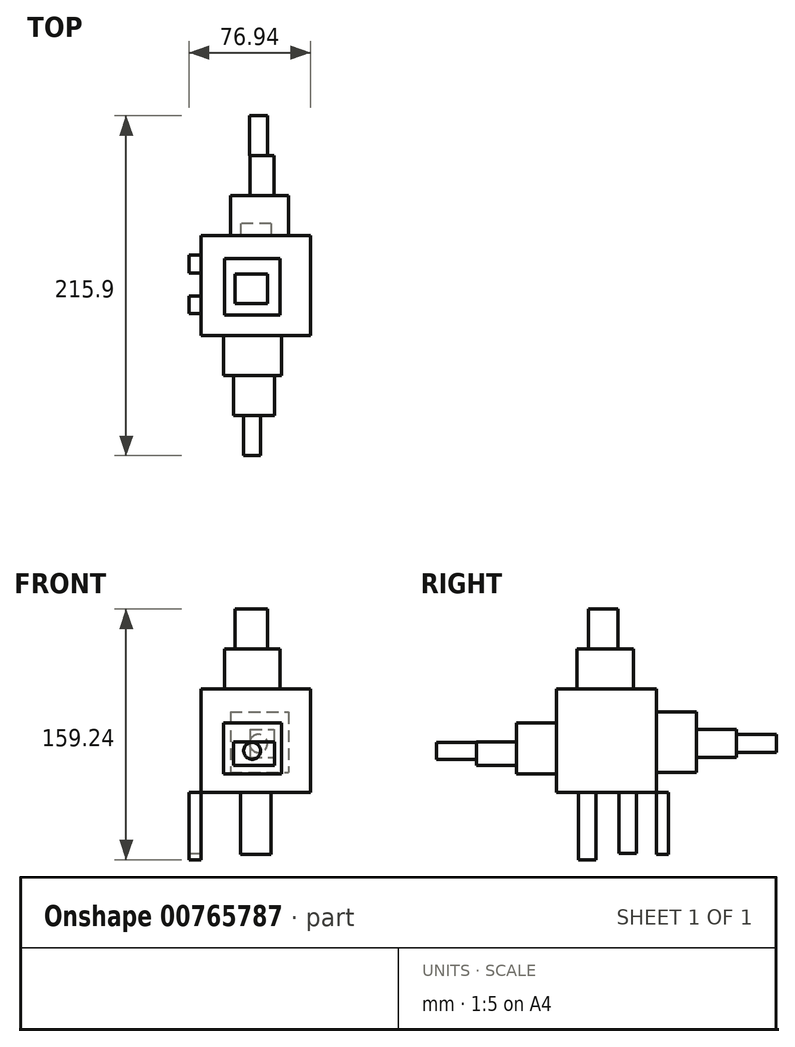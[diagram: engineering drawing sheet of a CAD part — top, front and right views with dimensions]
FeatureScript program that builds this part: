
annotation { "Feature Type Name" : "Feature", "Feature Type Description" : "" }
export const myFeature = defineFeature(function(context is Context, id is Id, definition is map)
    precondition{}
    {
        {
            var Q0;
            Q0=qCreatedBy(makeId("Front.planeOp"),FACE);
            var sketch = newSketch(context, id + "F0", { "sketchPlane" : qUnion([Q0])});
            skLineSegment(sketch, "E0.bottom", {"start": v(0, 0) * mm, "end": v(-69.32, 0) * mm});
            skLineSegment(sketch, "E0.top", {"start": v(0, 65.58) * mm, "end": v(-69.32, 65.58) * mm});
            skLineSegment(sketch, "E0.left", {"start": v(0, 0) * mm, "end": v(0, 65.58) * mm});
            skLineSegment(sketch, "E0.right", {"start": v(-69.32, 0) * mm, "end": v(-69.32, 65.58) * mm});
            skSolve(sketch);
        }
        {
            var Q0;
            Q0 = qSketchRegion(id + "F0", true);
            extrude(context, id + "F1", {"entities" : qUnion([Q0]), "depth" : 63.5 * mm, "offsetDistance" : 25.4 * mm});
        }
        {
            var Q0;
            Q0=makeQuery(id+"F1.opExtrude","SWEPT_FACE",FACE,{"disambiguationData":[OSD([sQuery(id+"F0.wireOp",EDGE,"E0.top")])]});
            var sketch = newSketch(context, id + "F2", { "sketchPlane" : qUnion([Q0])});
            skLineSegment(sketch, "E1.bottom", {"start": v(-54.41, -14.4) * mm, "end": v(-19.32, -14.4) * mm});
            skLineSegment(sketch, "E1.top", {"start": v(-54.41, -50.4) * mm, "end": v(-19.32, -50.4) * mm});
            skLineSegment(sketch, "E1.left", {"start": v(-54.41, -14.4) * mm, "end": v(-54.41, -50.4) * mm});
            skLineSegment(sketch, "E1.right", {"start": v(-19.32, -14.4) * mm, "end": v(-19.32, -50.4) * mm});
            skSolve(sketch);
        }
        {
            var Q0;
            Q0 = qSketchRegion(id + "F2", true);
            extrude(context, id + "F3", {"entities" : qUnion([Q0]), "operationType" : NewBodyOperationType.ADD, "depth" : 25.4 * mm, "offsetDistance" : 25.4 * mm});
        }
        {
            var Q0;
            Q0=makeQuery(id+"F3.opExtrude","CAP_FACE",FACE,{"disambiguationData":[OSD([sQuery(id+"F2.wireOp",EDGE,"E1.bottom"),sQuery(id+"F2.wireOp",EDGE,"E1.top"),sQuery(id+"F2.wireOp",EDGE,"E1.left"),sQuery(id+"F2.wireOp",EDGE,"E1.right")])],"isStart":false});
            var sketch = newSketch(context, id + "F4", { "sketchPlane" : qUnion([Q0])});
            skLineSegment(sketch, "E2.bottom", {"start": v(-47.96, -24.32) * mm, "end": v(-27.13, -24.32) * mm});
            skLineSegment(sketch, "E2.top", {"start": v(-47.96, -42.99) * mm, "end": v(-27.13, -42.99) * mm});
            skLineSegment(sketch, "E2.left", {"start": v(-47.96, -24.32) * mm, "end": v(-47.96, -42.99) * mm});
            skLineSegment(sketch, "E2.right", {"start": v(-27.13, -24.32) * mm, "end": v(-27.13, -42.99) * mm});
            skSolve(sketch);
        }
        {
            var Q0;
            Q0 = qSketchRegion(id + "F4", true);
            extrude(context, id + "F5", {"entities" : qUnion([Q0]), "operationType" : NewBodyOperationType.ADD, "depth" : 25.4 * mm, "offsetDistance" : 25.4 * mm});
        }
        {
            var Q0;
            Q0=makeQuery(id+"F1.opExtrude","CAP_FACE",FACE,{"disambiguationData":[OSD([sQuery(id+"F0.wireOp",EDGE,"E0.bottom"),sQuery(id+"F0.wireOp",EDGE,"E0.top"),sQuery(id+"F0.wireOp",EDGE,"E0.left"),sQuery(id+"F0.wireOp",EDGE,"E0.right")])],"isStart":false});
            var sketch = newSketch(context, id + "F6", { "sketchPlane" : qUnion([Q0])});
            skLineSegment(sketch, "E3.bottom", {"start": v(-55.1, 44.17) * mm, "end": v(-18.17, 44.17) * mm});
            skLineSegment(sketch, "E3.top", {"start": v(-55.1, 11.61) * mm, "end": v(-18.17, 11.61) * mm});
            skLineSegment(sketch, "E3.left", {"start": v(-55.1, 44.17) * mm, "end": v(-55.1, 11.61) * mm});
            skLineSegment(sketch, "E3.right", {"start": v(-18.17, 44.17) * mm, "end": v(-18.17, 11.61) * mm});
            skSolve(sketch);
        }
        {
            var Q0;
            Q0 = qSketchRegion(id + "F6", true);
            extrude(context, id + "F7", {"entities" : qUnion([Q0]), "operationType" : NewBodyOperationType.ADD, "depth" : 25.4 * mm, "offsetDistance" : 25.4 * mm});
        }
        {
            var Q0;
            Q0=makeQuery(id+"F7.opExtrude","CAP_FACE",FACE,{"disambiguationData":[OSD([sQuery(id+"F6.wireOp",EDGE,"E3.bottom"),sQuery(id+"F6.wireOp",EDGE,"E3.top"),sQuery(id+"F6.wireOp",EDGE,"E3.left"),sQuery(id+"F6.wireOp",EDGE,"E3.right")])],"isStart":false});
            var sketch = newSketch(context, id + "F8", { "sketchPlane" : qUnion([Q0])});
            skLineSegment(sketch, "E4.bottom", {"start": v(-48.92, 32.12) * mm, "end": v(-22.66, 32.12) * mm});
            skLineSegment(sketch, "E4.top", {"start": v(-48.92, 17) * mm, "end": v(-22.66, 17) * mm});
            skLineSegment(sketch, "E4.left", {"start": v(-48.92, 32.12) * mm, "end": v(-48.92, 17) * mm});
            skLineSegment(sketch, "E4.right", {"start": v(-22.66, 32.12) * mm, "end": v(-22.66, 17) * mm});
            skSolve(sketch);
        }
        {
            var Q0;
            Q0 = qSketchRegion(id + "F8", true);
            extrude(context, id + "F9", {"entities" : qUnion([Q0]), "operationType" : NewBodyOperationType.ADD, "depth" : 25.4 * mm, "offsetDistance" : 25.4 * mm});
        }
        {
            var Q0;
            Q0=makeQuery(id+"F9.opExtrude","CAP_FACE",FACE,{"disambiguationData":[OSD([sQuery(id+"F8.wireOp",EDGE,"E4.bottom"),sQuery(id+"F8.wireOp",EDGE,"E4.top"),sQuery(id+"F8.wireOp",EDGE,"E4.left"),sQuery(id+"F8.wireOp",EDGE,"E4.right")])],"isStart":false});
            var sketch = newSketch(context, id + "F10", { "sketchPlane" : qUnion([Q0])});
            skCircle(sketch, "E5", {"center": v(-36.99, 26.38) * mm, "radius": 5.37 * mm});
            skSolve(sketch);
        }
        {
            var Q0;
            Q0 = qSketchRegion(id + "F10", true);
            extrude(context, id + "F11", {"entities" : qUnion([Q0]), "operationType" : NewBodyOperationType.ADD, "depth" : 25.4 * mm, "offsetDistance" : 25.4 * mm});
        }
        {
            var Q0;
            Q0=makeQuery(id+"F1.opExtrude","CAP_FACE",FACE,{"disambiguationData":[OSD([sQuery(id+"F0.wireOp",EDGE,"E0.bottom"),sQuery(id+"F0.wireOp",EDGE,"E0.top"),sQuery(id+"F0.wireOp",EDGE,"E0.left"),sQuery(id+"F0.wireOp",EDGE,"E0.right")])],"isStart":true});
            var sketch = newSketch(context, id + "F12", { "sketchPlane" : qUnion([Q0])});
            skLineSegment(sketch, "E6.bottom", {"start": v(50.77, 50.96) * mm, "end": v(13.84, 50.96) * mm});
            skLineSegment(sketch, "E6.top", {"start": v(50.77, 12.78) * mm, "end": v(13.84, 12.78) * mm});
            skLineSegment(sketch, "E6.left", {"start": v(50.77, 50.96) * mm, "end": v(50.77, 12.78) * mm});
            skLineSegment(sketch, "E6.right", {"start": v(13.84, 50.96) * mm, "end": v(13.84, 12.78) * mm});
            skSolve(sketch);
        }
        {
            var Q0;
            Q0 = qSketchRegion(id + "F12", true);
            extrude(context, id + "F13", {"entities" : qUnion([Q0]), "operationType" : NewBodyOperationType.ADD, "depth" : 25.4 * mm, "offsetDistance" : 25.4 * mm});
        }
        {
            var Q0;
            Q0=makeQuery(id+"F13.opExtrude","CAP_FACE",FACE,{"disambiguationData":[OSD([sQuery(id+"F12.wireOp",EDGE,"E6.bottom"),sQuery(id+"F12.wireOp",EDGE,"E6.top"),sQuery(id+"F12.wireOp",EDGE,"E6.left"),sQuery(id+"F12.wireOp",EDGE,"E6.right")])],"isStart":false});
            var sketch = newSketch(context, id + "F14", { "sketchPlane" : qUnion([Q0])});
            skLineSegment(sketch, "E7.bottom", {"start": v(38.3, 39.91) * mm, "end": v(23.03, 39.91) * mm});
            skLineSegment(sketch, "E7.top", {"start": v(38.3, 22.18) * mm, "end": v(23.03, 22.18) * mm});
            skLineSegment(sketch, "E7.left", {"start": v(38.3, 39.91) * mm, "end": v(38.3, 22.18) * mm});
            skLineSegment(sketch, "E7.right", {"start": v(23.03, 39.91) * mm, "end": v(23.03, 22.18) * mm});
            skSolve(sketch);
        }
        {
            var Q0;
            Q0 = qSketchRegion(id + "F14", true);
            extrude(context, id + "F15", {"entities" : qUnion([Q0]), "operationType" : NewBodyOperationType.ADD, "depth" : 25.4 * mm, "offsetDistance" : 25.4 * mm});
        }
        {
            var Q0;
            Q0=makeQuery(id+"F15.opExtrude","CAP_FACE",FACE,{"disambiguationData":[OSD([sQuery(id+"F14.wireOp",EDGE,"E7.bottom"),sQuery(id+"F14.wireOp",EDGE,"E7.top"),sQuery(id+"F14.wireOp",EDGE,"E7.left"),sQuery(id+"F14.wireOp",EDGE,"E7.right")])],"isStart":false});
            var sketch = newSketch(context, id + "F16", { "sketchPlane" : qUnion([Q0])});
            skCircle(sketch, "E8", {"center": v(32.98, 31.04) * mm, "radius": 5.72 * mm});
            skPoint(sketch, "E8.centerSnap0", {"position": v(38.3, 31.04) * mm});
            skSolve(sketch);
        }
        {
            var Q0;
            Q0 = qSketchRegion(id + "F16", true);
            extrude(context, id + "F17", {"entities" : qUnion([Q0]), "operationType" : NewBodyOperationType.ADD, "depth" : 25.4 * mm, "offsetDistance" : 25.4 * mm});
        }
        {
            var Q0;
            Q0=makeQuery(id+"F1.opExtrude","SWEPT_FACE",FACE,{"disambiguationData":[OSD([sQuery(id+"F0.wireOp",EDGE,"E0.right")])]});
            var sketch = newSketch(context, id + "F18", { "sketchPlane" : qUnion([Q0])});
            skLineSegment(sketch, "E9.bottom", {"start": v(12.44, 0) * mm, "end": v(23.8, 0) * mm});
            skLineSegment(sketch, "E9.top", {"start": v(12.44, -38.77) * mm, "end": v(23.8, -38.77) * mm});
            skLineSegment(sketch, "E9.left", {"start": v(12.44, 0) * mm, "end": v(12.44, -38.77) * mm});
            skLineSegment(sketch, "E9.right", {"start": v(23.8, 0) * mm, "end": v(23.8, -38.77) * mm});
            skSolve(sketch);
        }
        {
            var Q0;
            Q0 = qSketchRegion(id + "F18", true);
            extrude(context, id + "F19", {"entities" : qUnion([Q0]), "depth" : 7.62 * mm, "offsetDistance" : 25.4 * mm});
        }
        {
            var Q0;
            Q0=makeQuery(id+"F1.opExtrude","SWEPT_FACE",FACE,{"disambiguationData":[OSD([sQuery(id+"F0.wireOp",EDGE,"E0.right")])]});
            var sketch = newSketch(context, id + "F20", { "sketchPlane" : qUnion([Q0])});
            skLineSegment(sketch, "E10.bottom", {"start": v(38.28, 0) * mm, "end": v(49.42, 0) * mm});
            skLineSegment(sketch, "E10.top", {"start": v(38.28, -42.86) * mm, "end": v(49.42, -42.86) * mm});
            skLineSegment(sketch, "E10.left", {"start": v(38.28, 0) * mm, "end": v(38.28, -42.86) * mm});
            skLineSegment(sketch, "E10.right", {"start": v(49.42, 0) * mm, "end": v(49.42, -42.86) * mm});
            skSolve(sketch);
        }
        {
            var Q0;
            Q0 = qSketchRegion(id + "F20", true);
            extrude(context, id + "F21", {"entities" : qUnion([Q0]), "depth" : 7.62 * mm, "offsetDistance" : 25.4 * mm});
        }
        {
            var Q0;
            Q0=makeQuery(id+"F1.opExtrude","CAP_FACE",FACE,{"disambiguationData":[OSD([sQuery(id+"F0.wireOp",EDGE,"E0.bottom"),sQuery(id+"F0.wireOp",EDGE,"E0.top"),sQuery(id+"F0.wireOp",EDGE,"E0.left"),sQuery(id+"F0.wireOp",EDGE,"E0.right")])],"isStart":true});
            var sketch = newSketch(context, id + "F22", { "sketchPlane" : qUnion([Q0])});
            skLineSegment(sketch, "E11.bottom", {"start": v(44.18, 0) * mm, "end": v(24.87, 0) * mm});
            skLineSegment(sketch, "E11.top", {"start": v(44.18, -39.55) * mm, "end": v(24.87, -39.55) * mm});
            skLineSegment(sketch, "E11.left", {"start": v(44.18, 0) * mm, "end": v(44.18, -39.55) * mm});
            skLineSegment(sketch, "E11.right", {"start": v(24.87, 0) * mm, "end": v(24.87, -39.55) * mm});
            skSolve(sketch);
        }
        {
            var Q0;
            Q0 = qSketchRegion(id + "F22", true);
            extrude(context, id + "F23", {"entities" : qUnion([Q0]), "depth" : 7.62 * mm, "offsetDistance" : 25.4 * mm});
        }
    });
